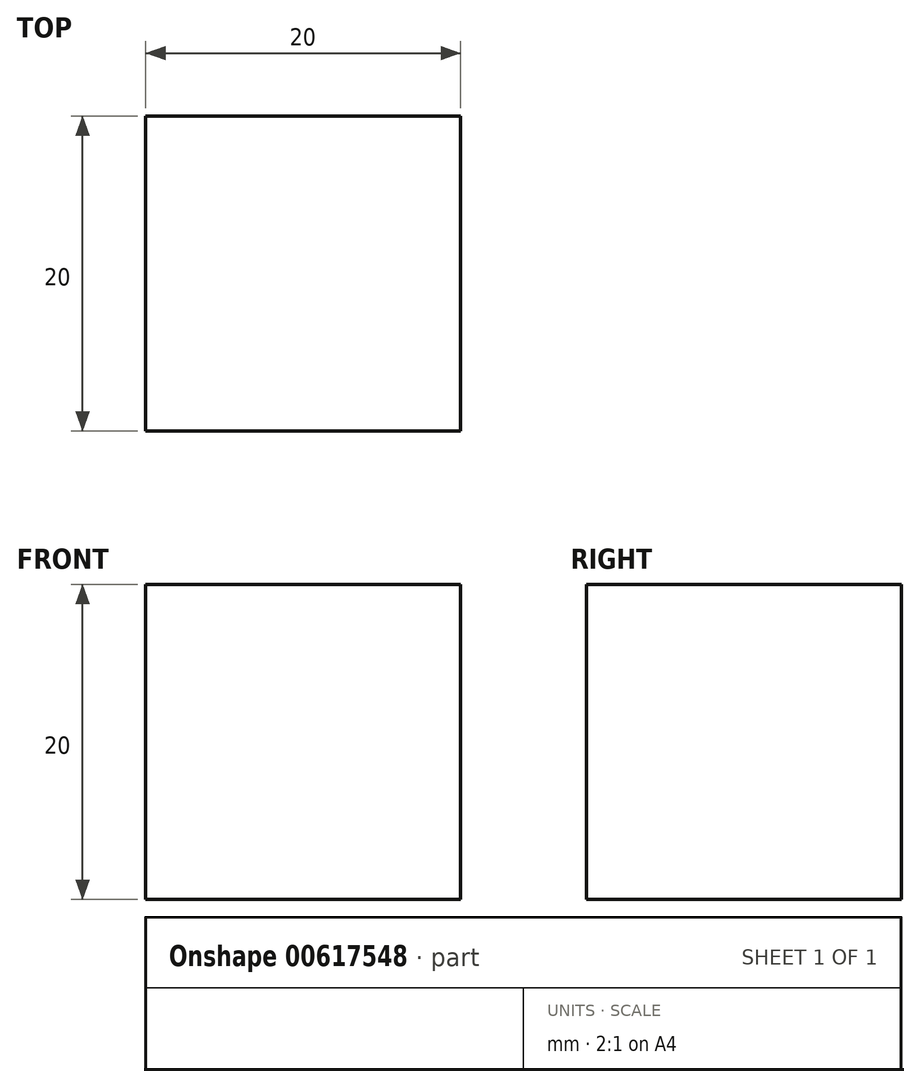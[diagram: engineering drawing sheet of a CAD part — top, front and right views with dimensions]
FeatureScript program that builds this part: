
annotation { "Feature Type Name" : "Feature", "Feature Type Description" : "" }
export const myFeature = defineFeature(function(context is Context, id is Id, definition is map)
    precondition{}
    {
        {
            var Q0;
            Q0=qCreatedBy(makeId("Front.planeOp"),FACE);
            var sketch = newSketch(context, id + "F0", { "sketchPlane" : qUnion([Q0])});
            skLineSegment(sketch, "E0.bottom", {"start": v(-6.5, 9.7) * mm, "end": v(13.5, 9.7) * mm});
            skLineSegment(sketch, "E0.top", {"start": v(-6.5, -10.3) * mm, "end": v(13.5, -10.3) * mm});
            skLineSegment(sketch, "E0.left", {"start": v(-6.5, 9.7) * mm, "end": v(-6.5, -10.3) * mm});
            skLineSegment(sketch, "E0.right", {"start": v(13.5, 9.7) * mm, "end": v(13.5, -10.3) * mm});
            skSolve(sketch);
        }
        {
            var Q0;
            Q0 = qSketchRegion(id + "F0", true);
            extrude(context, id + "F1", {"entities" : qUnion([Q0]), "depth" : 20 * mm, "offsetDistance" : 25 * mm});
        }
    });
